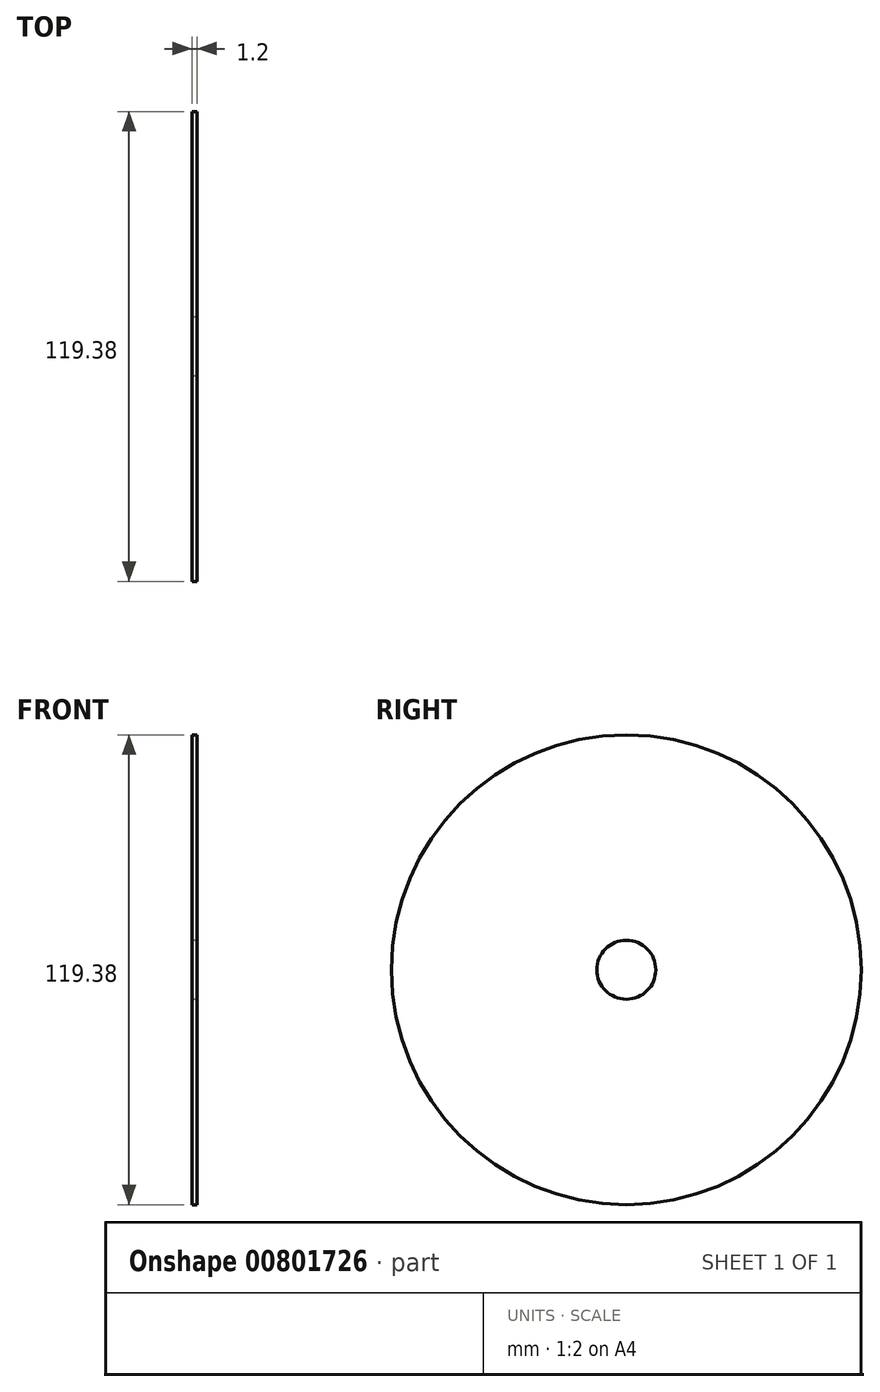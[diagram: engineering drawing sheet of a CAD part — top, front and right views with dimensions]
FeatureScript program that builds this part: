
annotation { "Feature Type Name" : "Feature", "Feature Type Description" : "" }
export const myFeature = defineFeature(function(context is Context, id is Id, definition is map)
    precondition{}
    {
        {
            var Q0;
            Q0=qCreatedBy(makeId("Right.planeOp"),FACE);
            var sketch = newSketch(context, id + "F0", { "sketchPlane" : qUnion([Q0])});
            skCircle(sketch, "E0", {"center": v(0, 0) * mm, "radius": 59.7 * mm});
            skCircle(sketch, "E1", {"center": v(0, 0) * mm, "radius": 7.5 * mm});
            skSolve(sketch);
        }
        {
            var Q0;
            Q0 = qSketchRegion(id + "F0", true);
            extrude(context, id + "F1", {"entities" : qUnion([Q0]), "depth" : 1.2 * mm, "offsetDistance" : 25.4 * mm});
        }
    });
